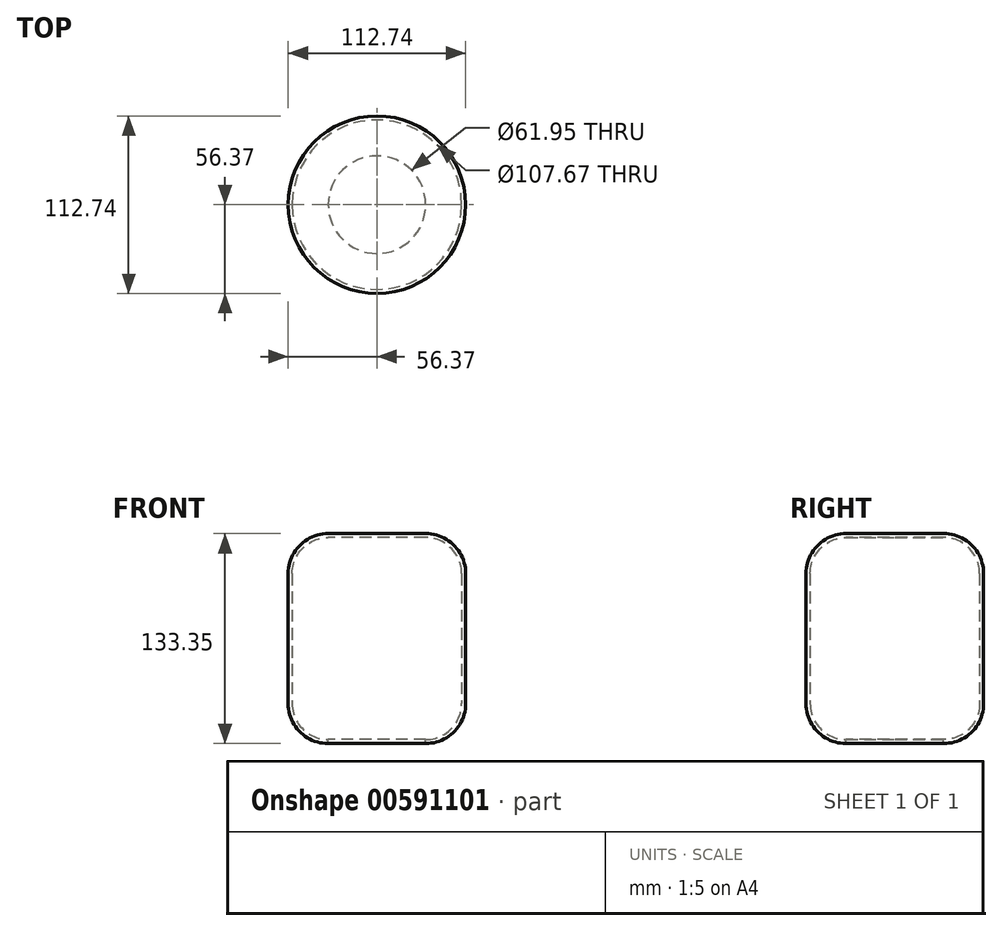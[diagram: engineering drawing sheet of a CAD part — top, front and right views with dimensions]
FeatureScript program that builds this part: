
annotation { "Feature Type Name" : "Feature", "Feature Type Description" : "" }
export const myFeature = defineFeature(function(context is Context, id is Id, definition is map)
    precondition{}
    {
        {
            var Q0;
            Q0=qCreatedBy(makeId("Top.planeOp"),FACE);
            var sketch = newSketch(context, id + "F0", { "sketchPlane" : qUnion([Q0])});
            skCircle(sketch, "E0", {"center": v(0, 0) * mm, "radius": 56.37 * mm});
            skSolve(sketch);
        }
        {
            var Q0;
            Q0 = qSketchRegion(id + "F0", true);
            extrude(context, id + "F1", {"entities" : qUnion([Q0]), "depth" : 133.35 * mm, "offsetDistance" : 25.4 * mm});
        }
        {
            var Q0;
            Q0=makeQuery(id+"F1.opExtrude","CAP_EDGE",EDGE,{"disambiguationData":[OSD([sQuery(id+"F0.wireOp",EDGE,"E0")])],"isStart":false});
            fillet(context, id + "F2", {"entities" : qUnion([Q0]), "radius" : 25.4 * mm, "tangentPropagation" : true, "allowEdgeOverflow" : false});
        }
        {
            var Q0;
            Q0=makeQuery(id+"F1.opExtrude","CAP_EDGE",EDGE,{"disambiguationData":[OSD([sQuery(id+"F0.wireOp",EDGE,"E0")])],"isStart":true});
            fillet(context, id + "F3", {"entities" : qUnion([Q0]), "radius" : 25.4 * mm, "tangentPropagation" : true, "allowEdgeOverflow" : false});
        }
        {
            var Q0;
            Q0=makeQuery(id+"F1.opExtrude","CAP_FACE",FACE,{"disambiguationData":[OSD([sQuery(id+"F0.wireOp",EDGE,"E0")])],"isStart":true});
            shell(context, id + "F4", {"entities" : qUnion([Q0]), "thickness" : 2.54 * mm});
        }
    });
